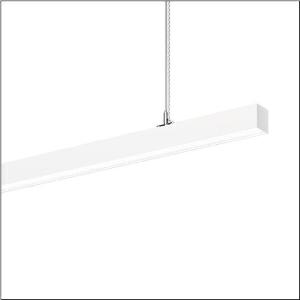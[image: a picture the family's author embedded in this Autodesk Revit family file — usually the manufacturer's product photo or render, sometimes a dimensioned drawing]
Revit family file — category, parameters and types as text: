
# Revit family: silica_r__21_51mx30da34wb_efde
name_source: partatom
category: Lighting Fixtures
units: mm (PartAtom-declared; Revit-internal decimal feet)

## family parameters
Cut with Voids When Loaded = No
Host = Face
Light Source = No
Part Type = Normal
Room Calculation Point = No
Round Connector Dimension = Use Diameter
Shared = No

## types (1)
- --- (1 x LED, 4210 lm, 27.7 W, 3000K)
    Apparent Load = 28 VA
    CIE Flux Codes = 47 79 96 57 100
    Color Rendering = 80
    Color Temperature = 3000K
    Default Elevation = 1800 mm
    Description = Silica® 21, office luminaire, primary optical cover: cover, of PMMA, opal, light emission: direct/indirect distribution, primary light characteristic: symmetric, installation type: suspended mounting, LED, rated luminous flux: 4.210lm, luminous efficacy: 152lm/W, light colour: 830, colour temperature: 3000K, with terminal, 3+2-pole, max. 2.5mm², mains connection: 220..240V, AC, 50/60Hz, rated input power: 27.7W, luminaire housing, of aluminium, traffic white (RAL 9016), length: 1.204mm, width: 53mm, height: 53mm, protection rating (complete): IP20, insulation class (complete): insulation class I (protective earthing), certification: CE, permissible operating ambient temperature: 0..+35°C, standard: EN 50419, packaging unit: 1 piece
    Height = 53 mm
    Lamp = 1 x LED
    Lamp Light Flux = 4210 lm
    Lamp Power = 27.7 W
    Lamp count = 1
    Length = 1204 mm
    Luminous efficacy = 152 lm/W
    Manufacturer = Siteco
    ModVariant = No
    Model = 51MX30DA34WB
    Mounting Place = Ceiling
    Mounting Type = Pendant
    Number of Poles = 1
    OnlyDefault = Yes
    Power Factor = 1
    Product Name = Silica® 21
    Product group = office luminaire | ceiling pendant
    ProductGroupID = 902
    Protection Class = Protection class I
    Protection Degree = IP 20
    RLX_Detail_Level = 1
    RLX_Emergency_Light_Flux = 0 lm
    RLX_Emergency_Type = 0
    RLX_Emergency_Type_DB = No
    RlxData = <blob elided: 21233 chars, md5=6b4fd30b>
    Socket = socket
    Standby Power = 0 W
    System Light Flux = 4210 lm
    System Power = 28 W
    Type Comments = factory setting: luminous flux: 100 % | dim-lin: 254 | 233 mA
    Type Image = l_1335916.jpg
    URL = http://relux.com
    VarID = @adj_086321
    Voltage = 0 V
    Weight = 0.00 kg
    Width = 53 mm

## geometry (parser evidence)
native form markers: Blend x4, Sweep x12
no freeform markers — native parametric forms only
